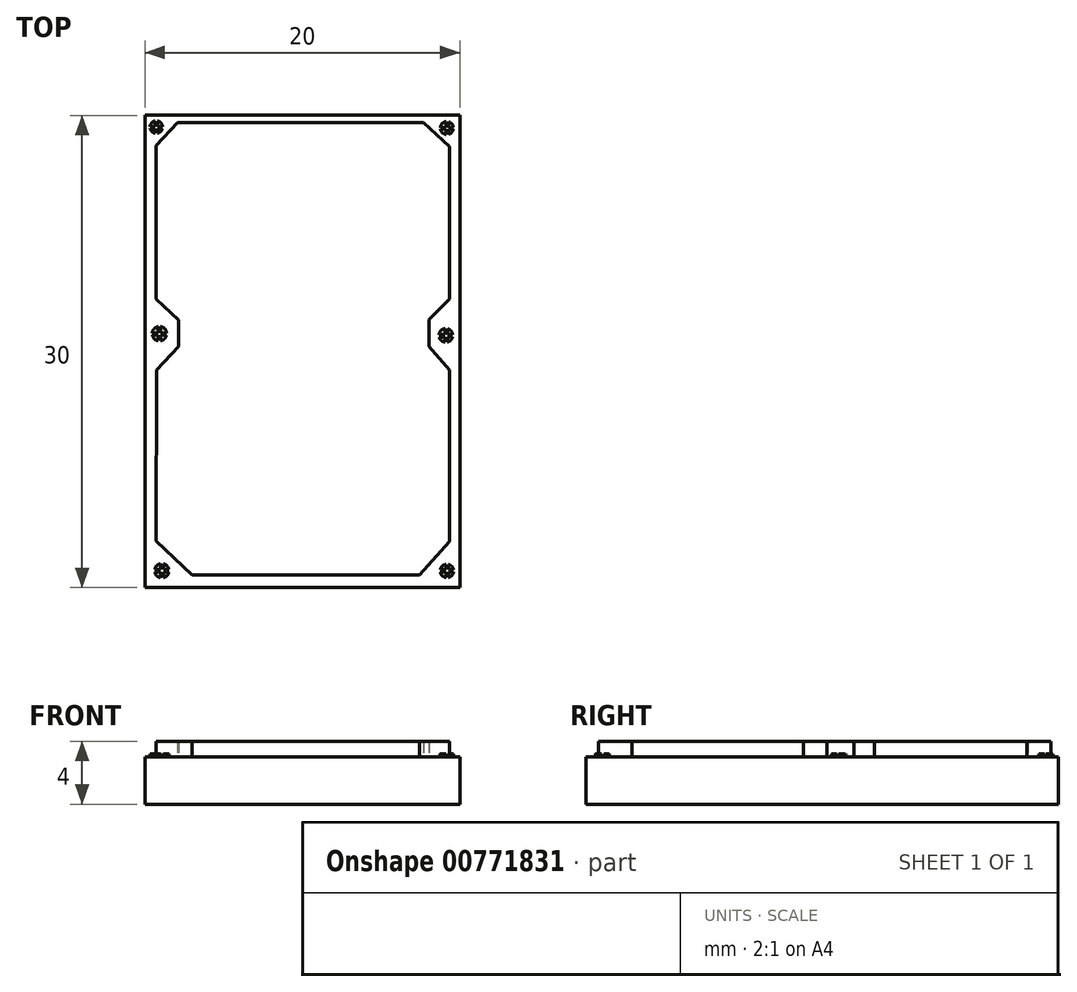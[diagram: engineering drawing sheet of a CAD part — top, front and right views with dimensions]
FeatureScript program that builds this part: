
annotation { "Feature Type Name" : "Feature", "Feature Type Description" : "" }
export const myFeature = defineFeature(function(context is Context, id is Id, definition is map)
    precondition{}
    {
        {
            var Q0;
            Q0=qCreatedBy(makeId("Top.planeOp"),FACE);
            var sketch = newSketch(context, id + "F0", { "sketchPlane" : qUnion([Q0])});
            skLineSegment(sketch, "E0.bottom", {"start": v(20, 43.51) * mm, "end": v(0, 43.51) * mm});
            skLineSegment(sketch, "E0.top", {"start": v(20, 13.51) * mm, "end": v(0, 13.51) * mm});
            skLineSegment(sketch, "E0.left", {"start": v(20, 43.51) * mm, "end": v(20, 13.51) * mm});
            skLineSegment(sketch, "E0.right", {"start": v(0, 43.51) * mm, "end": v(0, 13.51) * mm});
            skSolve(sketch);
        }
        {
            var Q0;
            Q0=makeQuery(id+"F0.imprint","IMPRINT",FACE,{"disambiguationData":[TD([[makeQuery(id+"F0.imprint","IMPRINT",EDGE,{"derivedFrom":sQuery(id+"F0.wireOp",EDGE,"E0.bottom")}),1.0]])]});
            extrude(context, id + "F1", {"entities" : qUnion([Q0]), "depth" : 3 * mm, "offsetDistance" : 25 * mm});
        }
        {
            var Q0;
            Q0=makeQuery(id+"F1.opExtrude","CAP_FACE",FACE,{"disambiguationData":[OSD([sQuery(id+"F0.wireOp",EDGE,"E0.bottom"),sQuery(id+"F0.wireOp",EDGE,"E0.top"),sQuery(id+"F0.wireOp",EDGE,"E0.left"),sQuery(id+"F0.wireOp",EDGE,"E0.right")])],"isStart":false});
            var sketch = newSketch(context, id + "F2", { "sketchPlane" : qUnion([Q0])});
            skLineSegment(sketch, "E1", {"start": v(17.7, 43.05) * mm, "end": v(19.34, 41.52) * mm});
            skLineSegment(sketch, "E2", {"start": v(19.34, 41.52) * mm, "end": v(19.34, 31.84) * mm});
            skLineSegment(sketch, "E3", {"start": v(19.34, 31.84) * mm, "end": v(18.06, 30.55) * mm});
            skLineSegment(sketch, "E4", {"start": v(18.06, 30.55) * mm, "end": v(18.06, 28.82) * mm});
            skLineSegment(sketch, "E5", {"start": v(19.34, 27.33) * mm, "end": v(19.34, 16.44) * mm});
            skLineSegment(sketch, "E6", {"start": v(17.7, 43.05) * mm, "end": v(2.06, 43.05) * mm});
            skLineSegment(sketch, "E7", {"start": v(0.69, 41.58) * mm, "end": v(0.69, 31.84) * mm});
            skLineSegment(sketch, "E8", {"start": v(2.98, 14.3) * mm, "end": v(17.45, 14.3) * mm});
            skLineSegment(sketch, "E9", {"start": v(18.06, 28.82) * mm, "end": v(19.34, 27.33) * mm});
            skLineSegment(sketch, "E10", {"start": v(2.06, 43.05) * mm, "end": v(0.69, 41.58) * mm});
            skLineSegment(sketch, "E11", {"start": v(0.69, 31.84) * mm, "end": v(2.12, 30.5) * mm});
            skLineSegment(sketch, "E12", {"start": v(2.12, 30.5) * mm, "end": v(2.12, 28.82) * mm});
            skLineSegment(sketch, "E13", {"start": v(2.12, 28.82) * mm, "end": v(0.74, 27.33) * mm});
            skLineSegment(sketch, "E14", {"start": v(0.74, 27.33) * mm, "end": v(0.7, 16.49) * mm});
            skPoint(sketch, "E15.orphan", {"position": v(19.34, 13.51) * mm});
            skPoint(sketch, "E16.trimOffspring.end.orphan", {"position": v(0.69, 13.51) * mm});
            skLineSegment(sketch, "E17", {"start": v(0.7, 16.49) * mm, "end": v(2.98, 14.3) * mm});
            skLineSegment(sketch, "E18", {"start": v(19.34, 16.44) * mm, "end": v(17.45, 14.3) * mm});
            skSolve(sketch);
        }
        {
            var Q0;
            Q0=makeQuery(id+"F2.imprint","IMPRINT",FACE,{"disambiguationData":[TD([[makeQuery(id+"F2.imprint","IMPRINT",EDGE,{"derivedFrom":sQuery(id+"F2.wireOp",EDGE,"E1")}),-1.0]])]});
            extrude(context, id + "F3", {"entities" : qUnion([Q0]), "operationType" : NewBodyOperationType.ADD, "depth" : 1 * mm, "offsetDistance" : 25 * mm});
        }
        {
            var Q0;
            Q0=makeQuery(id+"F1.opExtrude","CAP_FACE",FACE,{"disambiguationData":[OSD([sQuery(id+"F0.wireOp",EDGE,"E0.bottom"),sQuery(id+"F0.wireOp",EDGE,"E0.top"),sQuery(id+"F0.wireOp",EDGE,"E0.left"),sQuery(id+"F0.wireOp",EDGE,"E0.right")])],"isStart":false});
            var sketch = newSketch(context, id + "F4", { "sketchPlane" : qUnion([Q0])});
            skCircle(sketch, "E19", {"center": v(0.72, 42.77) * mm, "radius": 0.4 * mm});
            skCircle(sketch, "E20", {"center": v(19.17, 42.7) * mm, "radius": 0.41 * mm});
            skCircle(sketch, "E21", {"center": v(0.91, 29.64) * mm, "radius": 0.46 * mm});
            skCircle(sketch, "E22", {"center": v(19.1, 29.54) * mm, "radius": 0.44 * mm});
            skCircle(sketch, "E23", {"center": v(19.17, 14.57) * mm, "radius": 0.43 * mm});
            skCircle(sketch, "E24", {"center": v(1.07, 14.59) * mm, "radius": 0.45 * mm});
            skLineSegment(sketch, "E25", {"start": v(1, 15.03) * mm, "end": v(1, 14.66) * mm});
            skLineSegment(sketch, "E26", {"start": v(1.18, 14.14) * mm, "end": v(1.18, 14.52) * mm});
            skLineSegment(sketch, "E27", {"start": v(1.52, 14.66) * mm, "end": v(1.18, 14.66) * mm});
            skLineSegment(sketch, "E28", {"start": v(0.62, 14.52) * mm, "end": v(1, 14.52) * mm});
            skLineSegment(sketch, "E29", {"start": v(19.11, 15) * mm, "end": v(19.11, 14.67) * mm});
            skLineSegment(sketch, "E30", {"start": v(19.28, 14.98) * mm, "end": v(19.28, 14.66) * mm});
            skLineSegment(sketch, "E31", {"start": v(19.6, 14.66) * mm, "end": v(19.28, 14.66) * mm});
            skLineSegment(sketch, "E32", {"start": v(18.75, 14.52) * mm, "end": v(19.11, 14.52) * mm});
            skLineSegment(sketch, "E33.trimOffspring", {"start": v(19.11, 14.67) * mm, "end": v(18.76, 14.67) * mm});
            skLineSegment(sketch, "E34.trimOffspring", {"start": v(19.11, 14.52) * mm, "end": v(19.11, 14.15) * mm});
            skLineSegment(sketch, "E35.trimOffspring", {"start": v(19.28, 14.52) * mm, "end": v(19.6, 14.52) * mm});
            skLineSegment(sketch, "E36.trimOffspring", {"start": v(19.28, 14.52) * mm, "end": v(19.28, 14.16) * mm});
            skLineSegment(sketch, "E37.trimOffspring", {"start": v(1, 14.66) * mm, "end": v(0.62, 14.66) * mm});
            skLineSegment(sketch, "E38.trimOffspring", {"start": v(1.18, 14.52) * mm, "end": v(1.52, 14.52) * mm});
            skLineSegment(sketch, "E39.trimOffspring", {"start": v(1, 14.52) * mm, "end": v(1, 14.14) * mm});
            skLineSegment(sketch, "E40.trimOffspring", {"start": v(1.18, 14.66) * mm, "end": v(1.18, 15.03) * mm});
            skLineSegment(sketch, "E41", {"start": v(19.05, 29.97) * mm, "end": v(19.05, 29.59) * mm});
            skLineSegment(sketch, "E42", {"start": v(19.2, 29.11) * mm, "end": v(19.2, 29.44) * mm});
            skLineSegment(sketch, "E43", {"start": v(19.54, 29.59) * mm, "end": v(19.2, 29.59) * mm});
            skLineSegment(sketch, "E44", {"start": v(18.68, 29.44) * mm, "end": v(19.05, 29.44) * mm});
            skLineSegment(sketch, "E45.trimOffspring", {"start": v(19.05, 29.59) * mm, "end": v(18.68, 29.59) * mm});
            skLineSegment(sketch, "E46.trimOffspring", {"start": v(19.05, 29.44) * mm, "end": v(19.05, 29.1) * mm});
            skLineSegment(sketch, "E47.trimOffspring", {"start": v(19.2, 29.44) * mm, "end": v(19.53, 29.44) * mm});
            skLineSegment(sketch, "E48.trimOffspring", {"start": v(19.2, 29.59) * mm, "end": v(19.2, 29.96) * mm});
            skLineSegment(sketch, "E49", {"start": v(0.84, 30.1) * mm, "end": v(0.84, 29.68) * mm});
            skLineSegment(sketch, "E50", {"start": v(1, 29.2) * mm, "end": v(1, 29.55) * mm});
            skLineSegment(sketch, "E51", {"start": v(1, 30.1) * mm, "end": v(0.97, 30.11) * mm});
            skLineSegment(sketch, "E52", {"start": v(1.37, 29.68) * mm, "end": v(1, 29.68) * mm});
            skLineSegment(sketch, "E53", {"start": v(0.47, 29.55) * mm, "end": v(0.84, 29.55) * mm});
            skLineSegment(sketch, "E54.trimOffspring", {"start": v(0.84, 29.68) * mm, "end": v(0.46, 29.68) * mm});
            skLineSegment(sketch, "E55.trimOffspring", {"start": v(0.84, 29.55) * mm, "end": v(0.84, 29.2) * mm});
            skLineSegment(sketch, "E56.trimOffspring", {"start": v(1, 29.55) * mm, "end": v(1.36, 29.55) * mm});
            skLineSegment(sketch, "E57.trimOffspring", {"start": v(1, 29.68) * mm, "end": v(1, 30.1) * mm});
            skLineSegment(sketch, "E58", {"start": v(19.1, 43.1) * mm, "end": v(19.1, 42.74) * mm});
            skLineSegment(sketch, "E59", {"start": v(19.27, 42.3) * mm, "end": v(19.27, 42.63) * mm});
            skLineSegment(sketch, "E60", {"start": v(19.58, 42.74) * mm, "end": v(19.27, 42.74) * mm});
            skLineSegment(sketch, "E61", {"start": v(18.77, 42.63) * mm, "end": v(19.1, 42.63) * mm});
            skLineSegment(sketch, "E62", {"start": v(19.58, 42.63) * mm, "end": v(19.59, 42.66) * mm});
            skLineSegment(sketch, "E63.trimOffspring", {"start": v(19.1, 42.74) * mm, "end": v(18.76, 42.74) * mm});
            skLineSegment(sketch, "E64.trimOffspring", {"start": v(19.1, 42.63) * mm, "end": v(19.1, 42.3) * mm});
            skLineSegment(sketch, "E65.trimOffspring", {"start": v(19.27, 42.63) * mm, "end": v(19.58, 42.63) * mm});
            skLineSegment(sketch, "E66.trimOffspring", {"start": v(19.27, 42.74) * mm, "end": v(19.27, 43.1) * mm});
            skLineSegment(sketch, "E67", {"start": v(0.65, 43.16) * mm, "end": v(0.65, 42.81) * mm});
            skLineSegment(sketch, "E68", {"start": v(0.8, 42.38) * mm, "end": v(0.8, 43.16) * mm});
            skLineSegment(sketch, "E69", {"start": v(1.12, 42.81) * mm, "end": v(0.8, 42.81) * mm});
            skLineSegment(sketch, "E70", {"start": v(0.33, 42.68) * mm, "end": v(0.65, 42.68) * mm});
            skLineSegment(sketch, "E71", {"start": v(1.1, 42.68) * mm, "end": v(1.1, 42.65) * mm});
            skLineSegment(sketch, "E72.trimOffspring", {"start": v(0.65, 42.81) * mm, "end": v(0.32, 42.81) * mm});
            skLineSegment(sketch, "E73.trimOffspring", {"start": v(0.65, 42.68) * mm, "end": v(0.65, 42.37) * mm});
            skLineSegment(sketch, "E74.trimOffspring", {"start": v(0.8, 42.68) * mm, "end": v(1.1, 42.68) * mm});
            skSolve(sketch);
        }
        {
            var Q0;
            {var subQ0=sQuery(id+"F4.wireOp",EDGE,"E60");Q0=makeQuery(id+"F4.imprint","IMPRINT",FACE,{"disambiguationData":[TD([[makeQuery(id+"F4.imprint","IMPRINT",EDGE,{"derivedFrom":subQ0}),-1.0]])]});}
            var Q1;
            {var subQ0=sQuery(id+"F4.wireOp",EDGE,"E58");Q1=makeQuery(id+"F4.imprint","IMPRINT",FACE,{"disambiguationData":[TD([[makeQuery(id+"F4.imprint","IMPRINT",EDGE,{"derivedFrom":subQ0}),-1.0]])]});}
            var Q2;
            {var subQ0=sQuery(id+"F4.wireOp",EDGE,"E67");Q2=makeQuery(id+"F4.imprint","IMPRINT",FACE,{"disambiguationData":[TD([[makeQuery(id+"F4.imprint","IMPRINT",EDGE,{"derivedFrom":subQ0}),-1.0]])]});}
            var Q3;
            {var subQ3=sQuery(id+"F4.wireOp",EDGE,"E69");Q3=makeQuery(id+"F4.imprint","IMPRINT",FACE,{"disambiguationData":[TD([[makeQuery(id+"F4.imprint","IMPRINT",EDGE,{"derivedFrom":subQ3}),-1.0]])]});}
            var Q4;
            {var subQ3=sQuery(id+"F4.wireOp",EDGE,"E74.trimOffspring");Q4=makeQuery(id+"F4.imprint","IMPRINT",FACE,{"disambiguationData":[TD([[makeQuery(id+"F4.imprint","IMPRINT",EDGE,{"derivedFrom":subQ3}),-1.0]])]});}
            var Q5;
            {var subQ0=sQuery(id+"F4.wireOp",EDGE,"E70");Q5=makeQuery(id+"F4.imprint","IMPRINT",FACE,{"disambiguationData":[TD([[makeQuery(id+"F4.imprint","IMPRINT",EDGE,{"derivedFrom":subQ0}),-1.0]])]});}
            var Q6;
            {var subQ0=sQuery(id+"F4.wireOp",EDGE,"E61");Q6=makeQuery(id+"F4.imprint","IMPRINT",FACE,{"disambiguationData":[TD([[makeQuery(id+"F4.imprint","IMPRINT",EDGE,{"derivedFrom":subQ0}),-1.0]])]});}
            var Q7;
            {var subQ0=sQuery(id+"F4.wireOp",EDGE,"E59");Q7=makeQuery(id+"F4.imprint","IMPRINT",FACE,{"disambiguationData":[TD([[makeQuery(id+"F4.imprint","IMPRINT",EDGE,{"derivedFrom":subQ0}),-1.0]])]});}
            var Q8;
            {var subQ2=sQuery(id+"F4.wireOp",EDGE,"E52");Q8=makeQuery(id+"F4.imprint","IMPRINT",FACE,{"disambiguationData":[TD([[makeQuery(id+"F4.imprint","IMPRINT",EDGE,{"derivedFrom":subQ2}),-1.0]])]});}
            var Q9;
            {var subQ0=sQuery(id+"F4.wireOp",EDGE,"E49");Q9=makeQuery(id+"F4.imprint","IMPRINT",FACE,{"disambiguationData":[TD([[makeQuery(id+"F4.imprint","IMPRINT",EDGE,{"derivedFrom":subQ0}),-1.0]])]});}
            var Q10;
            {var subQ0=sQuery(id+"F4.wireOp",EDGE,"E53");Q10=makeQuery(id+"F4.imprint","IMPRINT",FACE,{"disambiguationData":[TD([[makeQuery(id+"F4.imprint","IMPRINT",EDGE,{"derivedFrom":subQ0}),-1.0]])]});}
            var Q11;
            {var subQ0=sQuery(id+"F4.wireOp",EDGE,"E50");Q11=makeQuery(id+"F4.imprint","IMPRINT",FACE,{"disambiguationData":[TD([[makeQuery(id+"F4.imprint","IMPRINT",EDGE,{"derivedFrom":subQ0}),-1.0]])]});}
            var Q12;
            {var subQ0=sQuery(id+"F4.wireOp",EDGE,"E43");Q12=makeQuery(id+"F4.imprint","IMPRINT",FACE,{"disambiguationData":[TD([[makeQuery(id+"F4.imprint","IMPRINT",EDGE,{"derivedFrom":subQ0}),-1.0]])]});}
            var Q13;
            {var subQ0=sQuery(id+"F4.wireOp",EDGE,"E41");Q13=makeQuery(id+"F4.imprint","IMPRINT",FACE,{"disambiguationData":[TD([[makeQuery(id+"F4.imprint","IMPRINT",EDGE,{"derivedFrom":subQ0}),-1.0]])]});}
            var Q14;
            {var subQ0=sQuery(id+"F4.wireOp",EDGE,"E44");Q14=makeQuery(id+"F4.imprint","IMPRINT",FACE,{"disambiguationData":[TD([[makeQuery(id+"F4.imprint","IMPRINT",EDGE,{"derivedFrom":subQ0}),-1.0]])]});}
            var Q15;
            {var subQ0=sQuery(id+"F4.wireOp",EDGE,"E42");Q15=makeQuery(id+"F4.imprint","IMPRINT",FACE,{"disambiguationData":[TD([[makeQuery(id+"F4.imprint","IMPRINT",EDGE,{"derivedFrom":subQ0}),-1.0]])]});}
            var Q16;
            {var subQ0=sQuery(id+"F4.wireOp",EDGE,"E25");Q16=makeQuery(id+"F4.imprint","IMPRINT",FACE,{"disambiguationData":[TD([[makeQuery(id+"F4.imprint","IMPRINT",EDGE,{"derivedFrom":subQ0}),-1.0]])]});}
            var Q17;
            {var subQ0=sQuery(id+"F4.wireOp",EDGE,"E27");Q17=makeQuery(id+"F4.imprint","IMPRINT",FACE,{"disambiguationData":[TD([[makeQuery(id+"F4.imprint","IMPRINT",EDGE,{"derivedFrom":subQ0}),-1.0]])]});}
            var Q18;
            {var subQ0=sQuery(id+"F4.wireOp",EDGE,"E26");Q18=makeQuery(id+"F4.imprint","IMPRINT",FACE,{"disambiguationData":[TD([[makeQuery(id+"F4.imprint","IMPRINT",EDGE,{"derivedFrom":subQ0}),-1.0]])]});}
            var Q19;
            {var subQ0=sQuery(id+"F4.wireOp",EDGE,"E28");Q19=makeQuery(id+"F4.imprint","IMPRINT",FACE,{"disambiguationData":[TD([[makeQuery(id+"F4.imprint","IMPRINT",EDGE,{"derivedFrom":subQ0}),-1.0]])]});}
            var Q20;
            {var subQ0=sQuery(id+"F4.wireOp",EDGE,"E30");Q20=makeQuery(id+"F4.imprint","IMPRINT",FACE,{"disambiguationData":[TD([[makeQuery(id+"F4.imprint","IMPRINT",EDGE,{"derivedFrom":subQ0}),1.0]])]});}
            var Q21;
            {var subQ0=sQuery(id+"F4.wireOp",EDGE,"E29");Q21=makeQuery(id+"F4.imprint","IMPRINT",FACE,{"disambiguationData":[TD([[makeQuery(id+"F4.imprint","IMPRINT",EDGE,{"derivedFrom":subQ0}),-1.0]])]});}
            var Q22;
            {var subQ0=sQuery(id+"F4.wireOp",EDGE,"E32");Q22=makeQuery(id+"F4.imprint","IMPRINT",FACE,{"disambiguationData":[TD([[makeQuery(id+"F4.imprint","IMPRINT",EDGE,{"derivedFrom":subQ0}),-1.0]])]});}
            var Q23;
            {var subQ0=sQuery(id+"F4.wireOp",EDGE,"E35.trimOffspring");Q23=makeQuery(id+"F4.imprint","IMPRINT",FACE,{"disambiguationData":[TD([[makeQuery(id+"F4.imprint","IMPRINT",EDGE,{"derivedFrom":subQ0}),-1.0]])]});}
            extrude(context, id + "F5", {"entities" : qUnion([Q0, Q1, Q2, Q3, Q4, Q5, Q6, Q7, Q8, Q9, Q10, Q11, Q12, Q13, Q14, Q15, Q16, Q17, Q18, Q19, Q20, Q21, Q22, Q23]), "operationType" : NewBodyOperationType.ADD, "depth" : 0.2 * mm, "offsetDistance" : 25 * mm});
        }
    });
